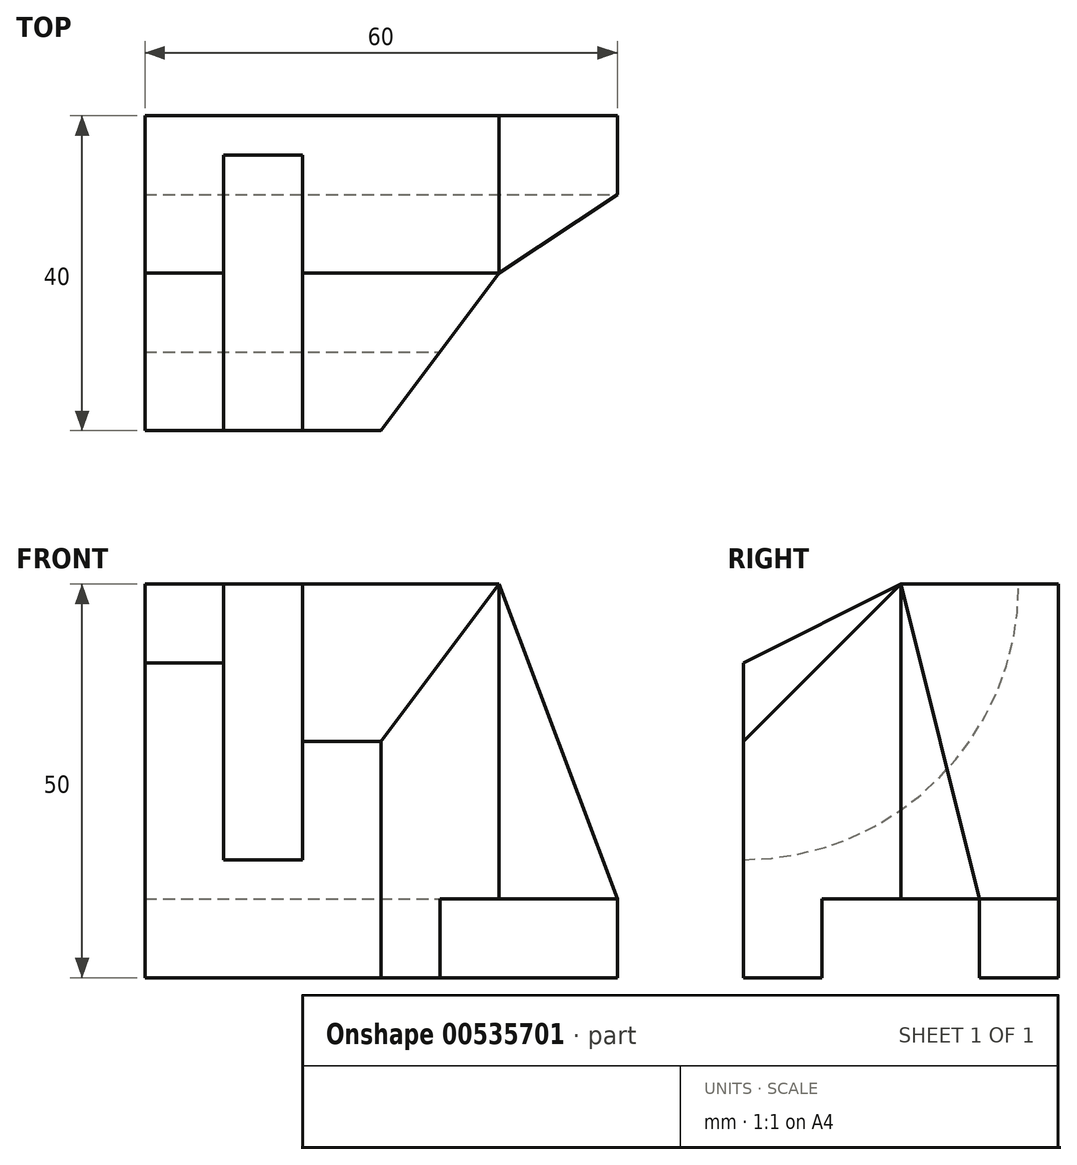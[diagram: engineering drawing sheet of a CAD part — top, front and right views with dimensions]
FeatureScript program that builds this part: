
annotation { "Feature Type Name" : "Feature", "Feature Type Description" : "" }
export const myFeature = defineFeature(function(context is Context, id is Id, definition is map)
    precondition{}
    {
        {
            var Q0;
            Q0=qCreatedBy(makeId("Top.planeOp"),FACE);
            var sketch = newSketch(context, id + "F0", { "sketchPlane" : qUnion([Q0])});
            skLineSegment(sketch, "E0.bottom", {"start": v(-38.8, 21.57) * mm, "end": v(21.2, 21.57) * mm});
            skLineSegment(sketch, "E0.top", {"start": v(-38.8, -18.43) * mm, "end": v(21.2, -18.43) * mm});
            skLineSegment(sketch, "E0.left", {"start": v(-38.8, 21.57) * mm, "end": v(-38.8, -18.43) * mm});
            skLineSegment(sketch, "E0.right", {"start": v(21.2, 21.57) * mm, "end": v(21.2, -18.43) * mm});
            skSolve(sketch);
        }
        {
            var Q0;
            Q0 = qSketchRegion(id + "F0", true);
            extrude(context, id + "F1", {"entities" : qUnion([Q0]), "depth" : 50 * mm, "offsetDistance" : 25 * mm});
        }
        {
            var Q0;
            Q0=makeQuery(id+"F1.opExtrude","SWEPT_FACE",FACE,{"disambiguationData":[OSD([sQuery(id+"F0.wireOp",EDGE,"E0.left")])]});
            cPlane(context, id + "F2", {"entities" : qUnion([Q0]), "cplaneType" : CPlaneType.OFFSET, "offset" : 10 * mm, "oppositeDirection" : true, "width" : 150 * mm, "height" : 150 * mm});
        }
        {
            var Q0;
            Q0=qCreatedBy(id+"F2.planeOp",FACE);
            var sketch = newSketch(context, id + "F3", { "sketchPlane" : qUnion([Q0])});
            skCircle(sketch, "E1", {"center": v(18.43, 50) * mm, "radius": 35 * mm});
            skSolve(sketch);
        }
        {
            var Q0;
            Q0 = qSketchRegion(id + "F3", true);
            extrude(context, id + "F4", {"entities" : qUnion([Q0]), "operationType" : NewBodyOperationType.REMOVE, "oppositeDirection" : true, "depth" : 10 * mm, "offsetDistance" : 25 * mm});
        }
        {
            var Q0;
            Q0=makeQuery(id+"F1.opExtrude","SWEPT_FACE",FACE,{"disambiguationData":[OSD([sQuery(id+"F0.wireOp",EDGE,"E0.left")])]});
            var sketch = newSketch(context, id + "F5", { "sketchPlane" : qUnion([Q0])});
            skLineSegment(sketch, "E2", {"start": v(-1.57, 50) * mm, "end": v(18.43, 50) * mm});
            skLineSegment(sketch, "E3", {"start": v(18.43, 50) * mm, "end": v(18.43, 40) * mm});
            skLineSegment(sketch, "E4", {"start": v(18.43, 40) * mm, "end": v(-1.57, 50) * mm});
            skSolve(sketch);
        }
        {
            var Q0;
            Q0 = qSketchRegion(id + "F5", true);
            extrude(context, id + "F6", {"entities" : qUnion([Q0]), "operationType" : NewBodyOperationType.REMOVE, "oppositeDirection" : true, "depth" : 10 * mm, "offsetDistance" : 25 * mm});
        }
        {
            var Q0;
            Q0=makeQuery(id+"F1.opExtrude","SWEPT_FACE",FACE,{"disambiguationData":[OSD([sQuery(id+"F0.wireOp",EDGE,"E0.right")])]});
            var sketch = newSketch(context, id + "F7", { "sketchPlane" : qUnion([Q0])});
            skLineSegment(sketch, "E5.bottom", {"start": v(-8.43, 10) * mm, "end": v(11.57, 10) * mm});
            skLineSegment(sketch, "E5.top", {"start": v(-8.43, 0) * mm, "end": v(11.57, 0) * mm});
            skLineSegment(sketch, "E5.left", {"start": v(-8.43, 10) * mm, "end": v(-8.43, 0) * mm});
            skLineSegment(sketch, "E5.right", {"start": v(11.57, 10) * mm, "end": v(11.57, 0) * mm});
            skSolve(sketch);
        }
        {
            var Q0;
            Q0 = qSketchRegion(id + "F7", true);
            extrude(context, id + "F8", {"entities" : qUnion([Q0]), "operationType" : NewBodyOperationType.REMOVE, "endBound" : BoundingType.UP_TO_NEXT, "oppositeDirection" : true, "depth" : 25 * mm, "offsetDistance" : 25 * mm});
        }
        {
            var Q0;
            Q0=makeQuery(id+"F1.opExtrude","CAP_FACE",FACE,{"disambiguationData":[OSD([sQuery(id+"F0.wireOp",EDGE,"E0.bottom"),sQuery(id+"F0.wireOp",EDGE,"E0.top"),sQuery(id+"F0.wireOp",EDGE,"E0.left"),sQuery(id+"F0.wireOp",EDGE,"E0.right")])],"isStart":false});
            var sketch = newSketch(context, id + "F9", { "sketchPlane" : qUnion([Q0])});
            skLineSegment(sketch, "E6", {"start": v(21.2, 11.57) * mm, "end": v(6.2, 1.57) * mm});
            skLineSegment(sketch, "E7", {"start": v(6.2, 1.57) * mm, "end": v(-8.8, -18.43) * mm});
            skLineSegment(sketch, "E8", {"start": v(-8.8, -18.43) * mm, "end": v(21.2, -18.43) * mm});
            skLineSegment(sketch, "E9", {"start": v(21.2, -18.43) * mm, "end": v(21.2, 11.57) * mm});
            skSolve(sketch);
        }
        {
            var Q0;
            Q0 = qSketchRegion(id + "F9", true);
            extrude(context, id + "F10", {"entities" : qUnion([Q0]), "operationType" : NewBodyOperationType.REMOVE, "endBound" : BoundingType.UP_TO_NEXT, "oppositeDirection" : true, "depth" : 25 * mm, "offsetDistance" : 25 * mm});
        }
        {
            var Q0;
            Q0=makeQuery(id+"F1.opExtrude","SWEPT_FACE",FACE,{"disambiguationData":[OSD([sQuery(id+"F0.wireOp",EDGE,"E0.bottom")])]});
            var sketch = newSketch(context, id + "F11", { "sketchPlane" : qUnion([Q0])});
            skLineSegment(sketch, "E10", {"start": v(-21.2, 50) * mm, "end": v(-6.2, 50) * mm});
            skLineSegment(sketch, "E11", {"start": v(-6.2, 50) * mm, "end": v(-21.2, 10) * mm});
            skLineSegment(sketch, "E12", {"start": v(-21.2, 10) * mm, "end": v(-21.2, 50) * mm});
            skSolve(sketch);
        }
        {
            var Q0;
            Q0 = qSketchRegion(id + "F11", true);
            extrude(context, id + "F12", {"entities" : qUnion([Q0]), "operationType" : NewBodyOperationType.REMOVE, "oppositeDirection" : true, "depth" : 25 * mm, "offsetDistance" : 25 * mm});
        }
        {
            var Q0;
            Q0=makeQuery(id+"F4.boolean.opBoolean","COPY",FACE,{"derivedFrom":makeQuery(id+"F4.opExtrude","CAP_FACE",FACE,{"disambiguationData":[OSD([sQuery(id+"F3.wireOp",EDGE,"E1")])],"isStart":false})});
            var sketch = newSketch(context, id + "F13", { "sketchPlane" : qUnion([Q0])});
            skLineSegment(sketch, "E13", {"start": v(-1.57, 50) * mm, "end": v(18.43, 50) * mm});
            skLineSegment(sketch, "E14", {"start": v(18.43, 50) * mm, "end": v(18.43, 30) * mm});
            skLineSegment(sketch, "E15", {"start": v(18.43, 30) * mm, "end": v(-1.57, 50) * mm});
            skSolve(sketch);
        }
        {
            var Q0;
            Q0 = qSketchRegion(id + "F13", true);
            extrude(context, id + "F14", {"entities" : qUnion([Q0]), "operationType" : NewBodyOperationType.REMOVE, "oppositeDirection" : true, "depth" : 25 * mm, "offsetDistance" : 25 * mm});
        }
    });
